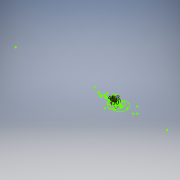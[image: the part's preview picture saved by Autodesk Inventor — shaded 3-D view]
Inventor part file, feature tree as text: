
AUTODESK INVENTOR PART (.ipt)
format: ipt  version: 2018 (Build 220112000, 112)  size: 326,656 bytes
history: native  units: mm
features: sketch x54, plane x13, revolve x1, extrude x1
ambient origin geometry x8: Origin, YZ Plane, XZ Plane, XY Plane, X Axis, Y Axis, Z Axis, Center Point
bodies: Body1 (feature_tree)
feature tree (69):
  sketch  "Sketch1"  dims[d10=50.0mm d21=40.0mm]
  sketch  "Sketch2"  dims[d22=38.0mm d65=46.0mm]
  sketch  "Sketch3"  dims[d66=48.3mm]
  sketch  "Sketch4"  dims[d87=30.0mm]
  sketch  "Sketch5"  dims[d167=180.0deg]
  sketch  "Sketch7"  dims[d168=3.0mm d169=0.0mm]
  sketch  "Sketch8"
  sketch  "Sketch9"
  sketch  "Sketch10"
  sketch  "Sketch11"
  sketch  "Sketch12"
  sketch  "Sketch13"
  sketch  "Sketch16"
  sketch  "Sketch18"
  sketch  "Sketch19"
  sketch  "Sketch20"
  sketch  "Sketch21"
  sketch  "Sketch22"
  sketch  "Sketch23"
  sketch  "Sketch24"
  sketch  "Sketch25"
  sketch  "Sketch31"
  sketch  "Sketch32"
  sketch  "Sketch34"
  sketch  "Sketch35"
  plane  "Work Plane16"
  sketch  "Sketch36"
  sketch  "Sketch37"
  sketch  "Sketch38"
  sketch  "Sketch39"
  sketch  "Sketch40"
  sketch  "Sketch41"
  plane  "Work Plane13"
  sketch  "Sketch43"
  plane  "Work Plane14"
  sketch  "Sketch45"
  sketch  "Sketch47"
  sketch  "Sketch48"
  sketch  "Sketch49"
  sketch  "Sketch50"
  sketch  "Sketch52"
  sketch  "Sketch53"
  sketch  "Sketch55"
  plane  "Work Plane5"
  sketch  "Sketch56"
  plane  "Work Plane3"
  plane  "Work Plane6"
  sketch  "Sketch57"
  plane  "Work Plane7"
  sketch  "Sketch58"
  plane  "Work Plane8"
  sketch  "Sketch59"
  sketch  "Sketch60"
  plane  "Work Plane9"
  sketch  "Sketch61"
  plane  "Work Plane10"
  sketch  "Sketch62"
  plane  "Work Plane12"
  sketch  "Sketch65"
  plane  "Work Plane11"
  sketch  "Sketch67"
  plane  "Work Plane15"
  sketch  "Sketch68"
  sketch  "Sketch69"
  sketch  "Sketch70"
  revolve  "Revolution5"  [1 undecoded]
  extrude  "Extrusion58"  Depth=46.0mm
  sketch  "Sketch71"
  sketch  "Sketch72"
note: 1 required parameter value undecoded (feature->parameter linkage not recoverable at this tier; creation-order binding heuristic only, values carry confidence <= 0.55)
